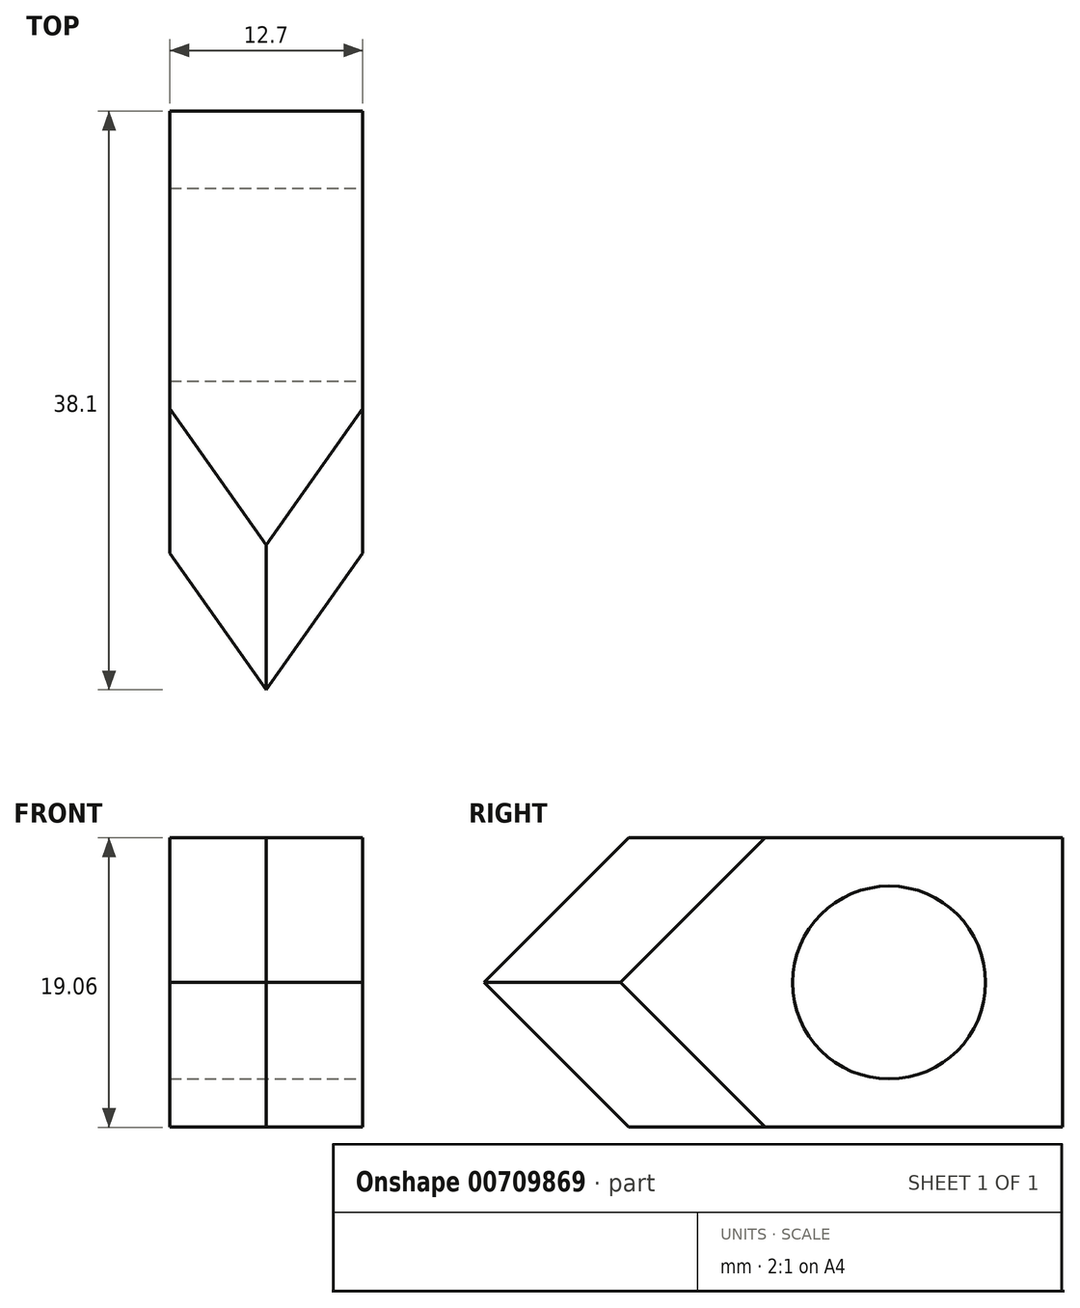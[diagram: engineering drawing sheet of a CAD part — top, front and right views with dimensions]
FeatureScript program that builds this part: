
annotation { "Feature Type Name" : "Feature", "Feature Type Description" : "" }
export const myFeature = defineFeature(function(context is Context, id is Id, definition is map)
    precondition{}
    {
        {
            var Q0;
            Q0=qCreatedBy(makeId("Front.planeOp"),FACE);
            var sketch = newSketch(context, id + "F0", { "sketchPlane" : qUnion([Q0])});
            skLineSegment(sketch, "E0.bottom", {"start": v(6.35, 9.53) * mm, "end": v(-6.35, 9.53) * mm});
            skLineSegment(sketch, "E0.top", {"start": v(6.35, -9.53) * mm, "end": v(-6.35, -9.53) * mm});
            skLineSegment(sketch, "E0.left", {"start": v(6.35, 9.53) * mm, "end": v(6.35, -9.53) * mm});
            skLineSegment(sketch, "E0.right", {"start": v(-6.35, 9.53) * mm, "end": v(-6.35, -9.53) * mm});
            skSolve(sketch);
        }
        {
            var Q0;
            Q0=makeQuery(id+"F0.imprint","IMPRINT",FACE,{"disambiguationData":[TD([[makeQuery(id+"F0.imprint","IMPRINT",EDGE,{"derivedFrom":sQuery(id+"F0.wireOp",EDGE,"E0.bottom")}),1.0]])]});
            extrude(context, id + "F1", {"entities" : qUnion([Q0]), "endBound" : BoundingType.SYMMETRIC, "depth" : 25.4 * mm, "offsetDistance" : 25.4 * mm});
        }
        {
            var Q0;
            Q0=makeQuery(id+"F1.opExtrude","CAP_FACE",FACE,{"disambiguationData":[OSD([sQuery(id+"F0.wireOp",EDGE,"E0.bottom"),sQuery(id+"F0.wireOp",EDGE,"E0.top"),sQuery(id+"F0.wireOp",EDGE,"E0.left"),sQuery(id+"F0.wireOp",EDGE,"E0.right")])],"isStart":false});
            var sketch = newSketch(context, id + "F2", { "sketchPlane" : qUnion([Q0])});
            skLineSegment(sketch, "E1.bottom", {"start": v(-6.35, 9.53) * mm, "end": v(6.35, 9.53) * mm});
            skLineSegment(sketch, "E1.top", {"start": v(-6.35, -9.53) * mm, "end": v(6.35, -9.53) * mm});
            skLineSegment(sketch, "E1.left", {"start": v(-6.35, 9.53) * mm, "end": v(-6.35, -9.53) * mm});
            skLineSegment(sketch, "E1.right", {"start": v(6.35, 9.53) * mm, "end": v(6.35, -9.53) * mm});
            skSolve(sketch);
        }
        {
            var Q0;
            Q0=makeQuery(id+"F2.imprint","IMPRINT",FACE,{"disambiguationData":[TD([[makeQuery(id+"F2.imprint","IMPRINT",EDGE,{"derivedFrom":sQuery(id+"F2.wireOp",EDGE,"E1.bottom")}),1.0]])]});
            extrude(context, id + "F3", {"entities" : qUnion([Q0]), "operationType" : NewBodyOperationType.ADD, "depth" : 12.7 * mm, "offsetDistance" : 25.4 * mm});
        }
        {
            var Q0;
            Q0=makeQuery(id+"F3.opExtrude","CAP_EDGE",EDGE,{"disambiguationData":[OSD([sQuery(id+"F2.wireOp",EDGE,"E1.bottom")])],"isStart":false});
            var Q1;
            Q1=makeQuery(id+"F3.opExtrude","CAP_EDGE",EDGE,{"disambiguationData":[OSD([sQuery(id+"F2.wireOp",EDGE,"E1.top")])],"isStart":false});
            chamfer(context, id + "F4", {"entities" : qUnion([Q0, Q1]), "width" : 9.52 * mm, "tangentPropagation" : true});
        }
        {
            var Q0;
            Q0=makeQuery(id+"F4.opChamfer","BLEND_EDGE",EDGE,{"blendedFrom":[makeQuery(id+"F3.opExtrude","CAP_EDGE",EDGE,{"disambiguationData":[OSD([sQuery(id+"F2.wireOp",EDGE,"E1.bottom")])],"isStart":false}),makeQuery(id+"F3.boolean.opBoolean","MERGE",FACE,{"derivedFrom":[makeQuery(id+"F1.opExtrude","SWEPT_FACE",FACE,{"disambiguationData":[OSD([sQuery(id+"F0.wireOp",EDGE,"E0.right")])]}),makeQuery(id+"F3.opExtrude","SWEPT_FACE",FACE,{"disambiguationData":[OSD([sQuery(id+"F2.wireOp",EDGE,"E1.left")])]})]})],"blendedInto":[makeQuery(id+"F3.boolean.opBoolean","MERGE",FACE,{"derivedFrom":[makeQuery(id+"F1.opExtrude","SWEPT_FACE",FACE,{"disambiguationData":[OSD([sQuery(id+"F0.wireOp",EDGE,"E0.right")])]}),makeQuery(id+"F3.opExtrude","SWEPT_FACE",FACE,{"disambiguationData":[OSD([sQuery(id+"F2.wireOp",EDGE,"E1.left")])]})]})]});
            var Q1;
            Q1=makeQuery(id+"F4.opChamfer","BLEND_EDGE",EDGE,{"blendedFrom":[makeQuery(id+"F3.opExtrude","CAP_EDGE",EDGE,{"disambiguationData":[OSD([sQuery(id+"F2.wireOp",EDGE,"E1.top")])],"isStart":false}),makeQuery(id+"F3.boolean.opBoolean","MERGE",FACE,{"derivedFrom":[makeQuery(id+"F1.opExtrude","SWEPT_FACE",FACE,{"disambiguationData":[OSD([sQuery(id+"F0.wireOp",EDGE,"E0.right")])]}),makeQuery(id+"F3.opExtrude","SWEPT_FACE",FACE,{"disambiguationData":[OSD([sQuery(id+"F2.wireOp",EDGE,"E1.left")])]})]})],"blendedInto":[makeQuery(id+"F3.boolean.opBoolean","MERGE",FACE,{"derivedFrom":[makeQuery(id+"F1.opExtrude","SWEPT_FACE",FACE,{"disambiguationData":[OSD([sQuery(id+"F0.wireOp",EDGE,"E0.right")])]}),makeQuery(id+"F3.opExtrude","SWEPT_FACE",FACE,{"disambiguationData":[OSD([sQuery(id+"F2.wireOp",EDGE,"E1.left")])]})]})]});
            var Q2;
            Q2=makeQuery(id+"F4.opChamfer","BLEND_EDGE",EDGE,{"blendedFrom":[makeQuery(id+"F3.opExtrude","CAP_EDGE",EDGE,{"disambiguationData":[OSD([sQuery(id+"F2.wireOp",EDGE,"E1.bottom")])],"isStart":false}),makeQuery(id+"F3.boolean.opBoolean","MERGE",FACE,{"derivedFrom":[makeQuery(id+"F1.opExtrude","SWEPT_FACE",FACE,{"disambiguationData":[OSD([sQuery(id+"F0.wireOp",EDGE,"E0.left")])]}),makeQuery(id+"F3.opExtrude","SWEPT_FACE",FACE,{"disambiguationData":[OSD([sQuery(id+"F2.wireOp",EDGE,"E1.right")])]})]})],"blendedInto":[makeQuery(id+"F3.boolean.opBoolean","MERGE",FACE,{"derivedFrom":[makeQuery(id+"F1.opExtrude","SWEPT_FACE",FACE,{"disambiguationData":[OSD([sQuery(id+"F0.wireOp",EDGE,"E0.left")])]}),makeQuery(id+"F3.opExtrude","SWEPT_FACE",FACE,{"disambiguationData":[OSD([sQuery(id+"F2.wireOp",EDGE,"E1.right")])]})]})]});
            var Q3;
            Q3=makeQuery(id+"F4.opChamfer","BLEND_EDGE",EDGE,{"blendedFrom":[makeQuery(id+"F3.opExtrude","CAP_EDGE",EDGE,{"disambiguationData":[OSD([sQuery(id+"F2.wireOp",EDGE,"E1.top")])],"isStart":false}),makeQuery(id+"F3.boolean.opBoolean","MERGE",FACE,{"derivedFrom":[makeQuery(id+"F1.opExtrude","SWEPT_FACE",FACE,{"disambiguationData":[OSD([sQuery(id+"F0.wireOp",EDGE,"E0.left")])]}),makeQuery(id+"F3.opExtrude","SWEPT_FACE",FACE,{"disambiguationData":[OSD([sQuery(id+"F2.wireOp",EDGE,"E1.right")])]})]})],"blendedInto":[makeQuery(id+"F3.boolean.opBoolean","MERGE",FACE,{"derivedFrom":[makeQuery(id+"F1.opExtrude","SWEPT_FACE",FACE,{"disambiguationData":[OSD([sQuery(id+"F0.wireOp",EDGE,"E0.left")])]}),makeQuery(id+"F3.opExtrude","SWEPT_FACE",FACE,{"disambiguationData":[OSD([sQuery(id+"F2.wireOp",EDGE,"E1.right")])]})]})]});
            chamfer(context, id + "F5", {"entities" : qUnion([Q0, Q1, Q2, Q3]), "width" : 6.35 * mm, "tangentPropagation" : true});
        }
        {
            var Q0;
            Q0=makeQuery(id+"F3.boolean.opBoolean","MERGE",FACE,{"derivedFrom":[makeQuery(id+"F1.opExtrude","SWEPT_FACE",FACE,{"disambiguationData":[OSD([sQuery(id+"F0.wireOp",EDGE,"E0.left")])]}),makeQuery(id+"F3.opExtrude","SWEPT_FACE",FACE,{"disambiguationData":[OSD([sQuery(id+"F2.wireOp",EDGE,"E1.right")])]})]});
            var sketch = newSketch(context, id + "F6", { "sketchPlane" : qUnion([Q0])});
            skCircle(sketch, "E2", {"center": v(1.27, 0) * mm, "radius": 6.35 * mm});
            skSolve(sketch);
        }
        {
            var Q0;
            Q0=makeQuery(id+"F6.imprint","IMPRINT",FACE,{"disambiguationData":[TD([[makeQuery(id+"F6.imprint","IMPRINT",EDGE,{"derivedFrom":sQuery(id+"F6.wireOp",EDGE,"E2")}),1.0]])]});
            var Q1;
            Q1=sQuery(id+"F6.wireOp",EDGE,"E2");
            extrude(context, id + "F7", {"entities" : qUnion([Q0]), "operationType" : NewBodyOperationType.REMOVE, "surfaceEntities" : qUnion([Q1]), "oppositeDirection" : true, "depth" : 12.7 * mm, "offsetDistance" : 25.4 * mm});
        }
    });
